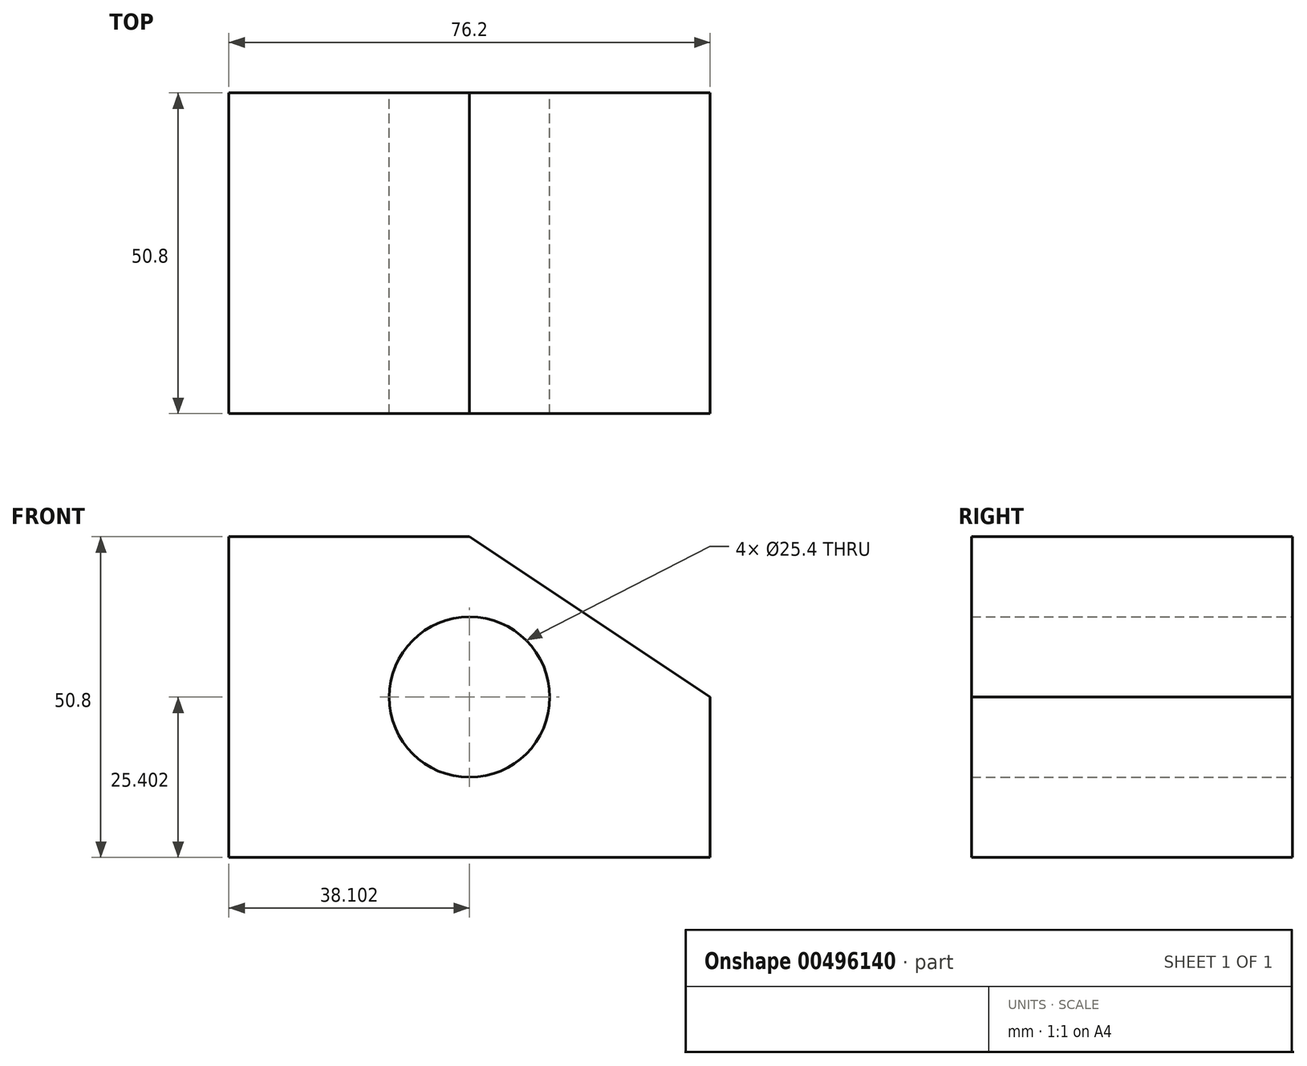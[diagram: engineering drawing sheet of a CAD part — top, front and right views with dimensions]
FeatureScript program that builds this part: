
annotation { "Feature Type Name" : "Feature", "Feature Type Description" : "" }
export const myFeature = defineFeature(function(context is Context, id is Id, definition is map)
    precondition{}
    {
        {
            var Q0;
            Q0=qCreatedBy(makeId("Front.planeOp"),FACE);
            var sketch = newSketch(context, id + "F0", { "sketchPlane" : qUnion([Q0])});
            skLineSegment(sketch, "E0.bottom", {"start": v(-23.48, 20.31) * mm, "end": v(52.72, 20.31) * mm});
            skLineSegment(sketch, "E0.top", {"start": v(-23.48, -30.49) * mm, "end": v(52.72, -30.49) * mm});
            skLineSegment(sketch, "E0.left", {"start": v(-23.48, 20.31) * mm, "end": v(-23.48, -30.49) * mm});
            skLineSegment(sketch, "E0.right", {"start": v(52.72, 20.31) * mm, "end": v(52.72, -30.49) * mm});
            skLineSegment(sketch, "E1", {"start": v(14.62, 20.31) * mm, "end": v(52.72, -5.09) * mm});
            skSolve(sketch);
        }
        {
            var Q0;
            {var subQ1=sQuery(id+"F0.wireOp",EDGE,"E0.top");Q0=makeQuery(id+"F0.imprint","IMPRINT",FACE,{"disambiguationData":[TD([[makeQuery(id+"F0.imprint","IMPRINT",EDGE,{"derivedFrom":subQ1}),1.0]])]});}
            extrude(context, id + "F1", {"entities" : qUnion([Q0]), "depth" : 50.8 * mm});
        }
        {
            var Q0;
            Q0=qCreatedBy(makeId("Front.planeOp"),FACE);
            var sketch = newSketch(context, id + "F2", { "sketchPlane" : qUnion([Q0])});
            skCircle(sketch, "E2", {"center": v(14.62, -5.09) * mm, "radius": 12.7 * mm});
            skSolve(sketch);
        }
        {
            var Q0;
            Q0 = qSketchRegion(id + "F2", true);
            extrude(context, id + "F3", {"entities" : qUnion([Q0]), "operationType" : NewBodyOperationType.REMOVE, "depth" : 50.8 * mm});
        }
    });
